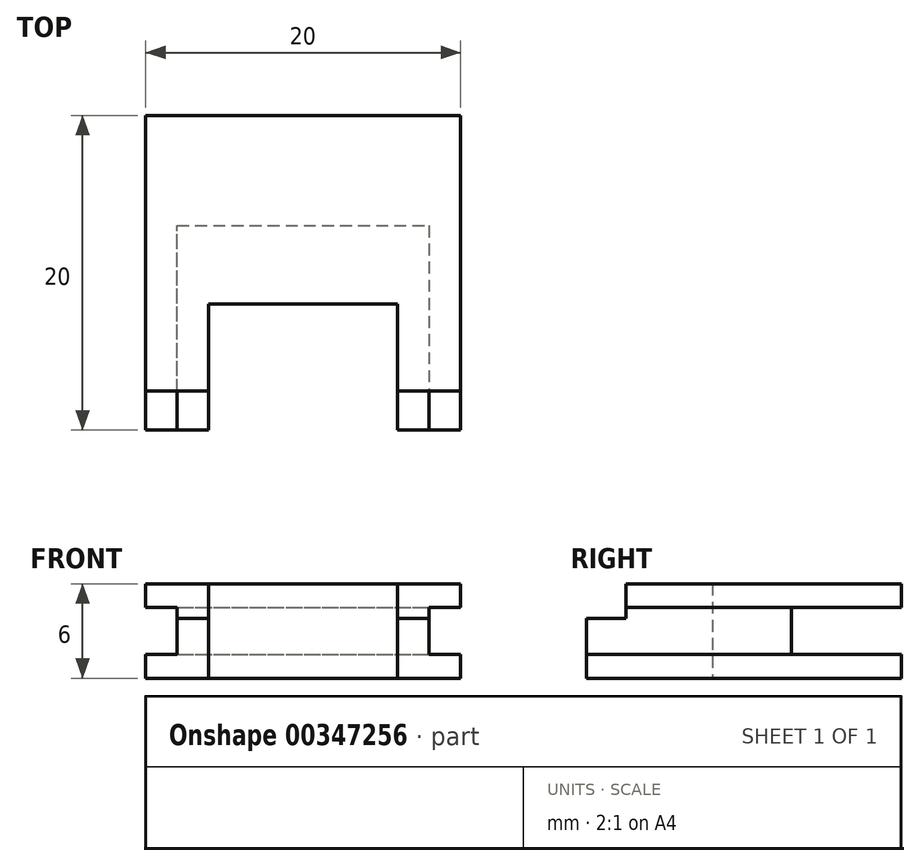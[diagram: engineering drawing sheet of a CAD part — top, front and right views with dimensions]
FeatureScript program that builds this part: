
annotation { "Feature Type Name" : "Feature", "Feature Type Description" : "" }
export const myFeature = defineFeature(function(context is Context, id is Id, definition is map)
    precondition{}
    {
        {
            var Q0;
            Q0=qCreatedBy(makeId("Top.planeOp"),FACE);
            var sketch = newSketch(context, id + "F0", { "sketchPlane" : qUnion([Q0])});
            skLineSegment(sketch, "E0", {"start": v(-10, 12) * mm, "end": v(10, 12) * mm});
            skLineSegment(sketch, "E1", {"start": v(10, 12) * mm, "end": v(10, -8) * mm});
            skLineSegment(sketch, "E2", {"start": v(10, -8) * mm, "end": v(6, -8) * mm});
            skLineSegment(sketch, "E3", {"start": v(6, -8) * mm, "end": v(6, 0) * mm});
            skLineSegment(sketch, "E4", {"start": v(6, 0) * mm, "end": v(-6, 0) * mm});
            skLineSegment(sketch, "E5", {"start": v(-6, 0) * mm, "end": v(-6, -8) * mm});
            skLineSegment(sketch, "E6", {"start": v(-6, -8) * mm, "end": v(-10, -8) * mm});
            skLineSegment(sketch, "E7", {"start": v(-10, -8) * mm, "end": v(-10, 12) * mm});
            skPoint(sketch, "E8", {"position": v(0, 0) * mm});
            skSolve(sketch);
        }
        {
            var Q0;
            Q0=makeQuery(id+"F0.imprint","IMPRINT",FACE,{"disambiguationData":[TD([[makeQuery(id+"F0.imprint","IMPRINT",EDGE,{"derivedFrom":sQuery(id+"F0.wireOp",EDGE,"E0")}),-1.0]])]});
            var Q1;
            Q1 = qSketchRegion(id + "F2", true);
            extrude(context, id + "F1", {"entities" : qUnion([Q0, Q1]), "offsetDistance" : 25 * mm, "depth" : 1.5 * mm});
        }
        {
            var Q0;
            Q0=makeQuery(id+"F1.opExtrude","CAP_FACE",FACE,{"disambiguationData":[OSD([sQuery(id+"F0.wireOp",EDGE,"E0"),sQuery(id+"F0.wireOp",EDGE,"E1"),sQuery(id+"F0.wireOp",EDGE,"E2"),sQuery(id+"F0.wireOp",EDGE,"E3"),sQuery(id+"F0.wireOp",EDGE,"E4"),sQuery(id+"F0.wireOp",EDGE,"E5"),sQuery(id+"F0.wireOp",EDGE,"E6"),sQuery(id+"F0.wireOp",EDGE,"E7")])],"isStart":false});
            var sketch = newSketch(context, id + "F2", { "sketchPlane" : qUnion([Q0])});
            skLineSegment(sketch, "E9", {"start": v(-8, -8) * mm, "end": v(-8, 5) * mm});
            skLineSegment(sketch, "E10", {"start": v(-8, 5) * mm, "end": v(8, 5) * mm});
            skLineSegment(sketch, "E11", {"start": v(8, 5) * mm, "end": v(8, -8) * mm});
            skSolve(sketch);
        }
        {
            var Q0;
            {var subQ2=sQuery(id+"F2.wireOp",EDGE,"E9");Q0=makeQuery(id+"F2.imprint","IMPRINT",FACE,{"disambiguationData":[TD([[makeQuery(id+"F2.imprint","IMPRINT",EDGE,{"derivedFrom":subQ2}),-1.0]])]});}
            extrude(context, id + "F3", {"entities" : qUnion([Q0]), "operationType" : NewBodyOperationType.ADD, "offsetDistance" : 25 * mm, "depth" : 3 * mm});
        }
        {
            var Q0;
            Q0=makeQuery(id+"F3.opExtrude","CAP_FACE",FACE,{"disambiguationData":[OSD([sQuery(id+"F0.wireOp",EDGE,"E2"),sQuery(id+"F0.wireOp",EDGE,"E3"),sQuery(id+"F0.wireOp",EDGE,"E4"),sQuery(id+"F0.wireOp",EDGE,"E5"),sQuery(id+"F0.wireOp",EDGE,"E6"),sQuery(id+"F2.wireOp",EDGE,"E9"),sQuery(id+"F2.wireOp",EDGE,"E10"),sQuery(id+"F2.wireOp",EDGE,"E11")])],"isStart":false});
            var sketch = newSketch(context, id + "F4", { "sketchPlane" : qUnion([Q0])});
            skLineSegment(sketch, "E12", {"start": v(-6, -8) * mm, "end": v(-10, -8) * mm});
            skPoint(sketch, "E12.endSnap0", {"position": v(-7, -8) * mm});
            skLineSegment(sketch, "E13", {"start": v(-10, -8) * mm, "end": v(-10, 12) * mm});
            skLineSegment(sketch, "E14", {"start": v(-10, 12) * mm, "end": v(10, 12) * mm});
            skLineSegment(sketch, "E15", {"start": v(10, 12) * mm, "end": v(10, -8) * mm});
            skLineSegment(sketch, "E16", {"start": v(10, -8) * mm, "end": v(6, -8) * mm});
            skLineSegment(sketch, "E17", {"start": v(6, -8) * mm, "end": v(6, 0) * mm});
            skLineSegment(sketch, "E18", {"start": v(6, 0) * mm, "end": v(-6, 0) * mm});
            skLineSegment(sketch, "E19", {"start": v(-6, 0) * mm, "end": v(-6, -8) * mm});
            skSolve(sketch);
        }
        {
            var Q0;
            {var subQ0=sQuery(id+"F4.wireOp",EDGE,"E17");Q0=makeQuery(id+"F4.imprint","IMPRINT",FACE,{"disambiguationData":[TD([[makeQuery(id+"F4.imprint","IMPRINT",EDGE,{"derivedFrom":subQ0}),-1.0]])]});}
            var Q1;
            {var subQ1=sQuery(id+"F4.wireOp",EDGE,"E13");Q1=makeQuery(id+"F4.imprint","IMPRINT",FACE,{"disambiguationData":[TD([[makeQuery(id+"F4.imprint","IMPRINT",EDGE,{"derivedFrom":subQ1}),-1.0]])]});}
            extrude(context, id + "F5", {"entities" : qUnion([Q0, Q1]), "operationType" : NewBodyOperationType.ADD, "offsetDistance" : 25 * mm, "depth" : 1.5 * mm});
        }
        {
            var Q0;
            Q0=makeQuery(id+"F5.opExtrude","CAP_FACE",FACE,{"disambiguationData":[OSD([sQuery(id+"F4.wireOp",EDGE,"E12"),sQuery(id+"F4.wireOp",EDGE,"E13"),sQuery(id+"F4.wireOp",EDGE,"E14"),sQuery(id+"F4.wireOp",EDGE,"E15"),sQuery(id+"F4.wireOp",EDGE,"E16"),sQuery(id+"F4.wireOp",EDGE,"E17"),sQuery(id+"F4.wireOp",EDGE,"E18"),sQuery(id+"F4.wireOp",EDGE,"E19")])],"isStart":false});
            var sketch = newSketch(context, id + "F6", { "sketchPlane" : qUnion([Q0])});
            skLineSegment(sketch, "E20.bottom", {"start": v(6, -5.5) * mm, "end": v(10, -5.5) * mm});
            skLineSegment(sketch, "E20.top", {"start": v(6, -8) * mm, "end": v(10, -8) * mm});
            skLineSegment(sketch, "E20.left", {"start": v(6, -5.5) * mm, "end": v(6, -8) * mm});
            skLineSegment(sketch, "E20.right", {"start": v(10, -5.5) * mm, "end": v(10, -8) * mm});
            skLineSegment(sketch, "E21.bottom", {"start": v(-6, -5.5) * mm, "end": v(-10, -5.5) * mm});
            skLineSegment(sketch, "E21.top", {"start": v(-6, -8) * mm, "end": v(-10, -8) * mm});
            skLineSegment(sketch, "E21.left", {"start": v(-6, -5.5) * mm, "end": v(-6, -8) * mm});
            skLineSegment(sketch, "E21.right", {"start": v(-10, -5.5) * mm, "end": v(-10, -8) * mm});
            skSolve(sketch);
        }
        {
            var Q0;
            Q0=makeQuery(id+"F6.imprint","IMPRINT",FACE,{"disambiguationData":[TD([[makeQuery(id+"F6.imprint","IMPRINT",EDGE,{"derivedFrom":sQuery(id+"F6.wireOp",EDGE,"E21.bottom")}),1.0]])]});
            var Q1;
            Q1=makeQuery(id+"F6.imprint","IMPRINT",FACE,{"disambiguationData":[TD([[makeQuery(id+"F6.imprint","IMPRINT",EDGE,{"derivedFrom":sQuery(id+"F6.wireOp",EDGE,"E20.bottom")}),-1.0]])]});
            extrude(context, id + "F7", {"entities" : qUnion([Q0, Q1]), "operationType" : NewBodyOperationType.REMOVE, "oppositeDirection" : true, "offsetDistance" : 25 * mm, "depth" : 2.2 * mm});
        }
    });
